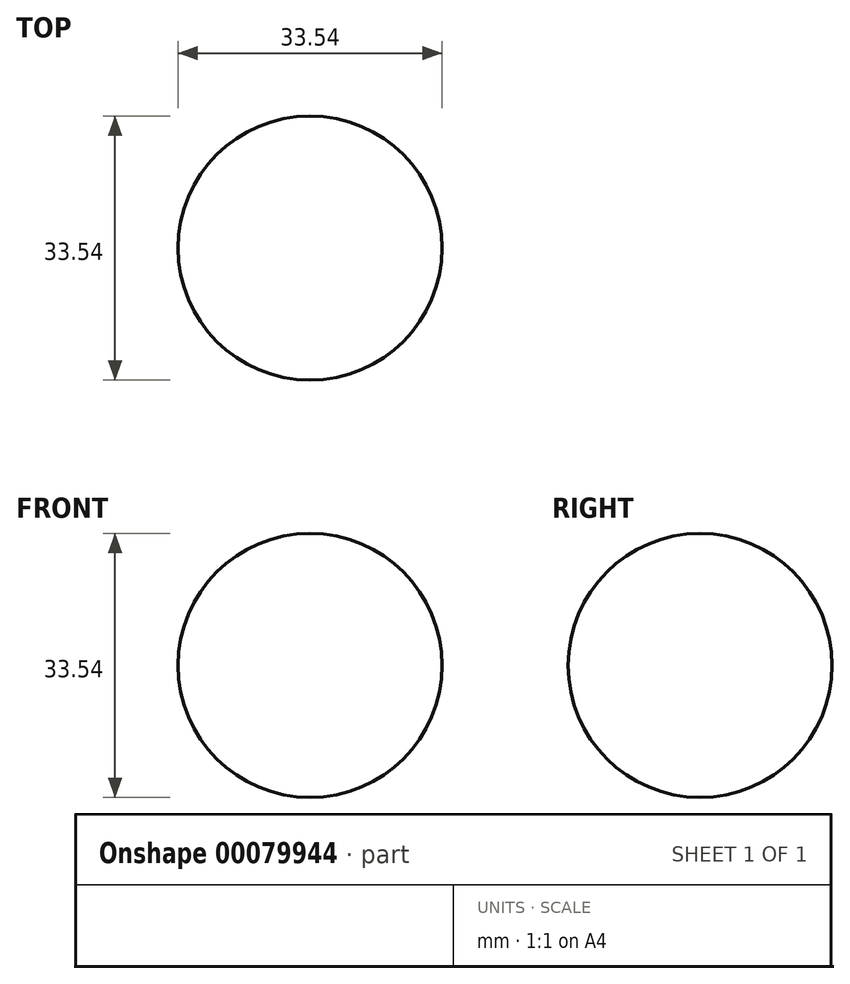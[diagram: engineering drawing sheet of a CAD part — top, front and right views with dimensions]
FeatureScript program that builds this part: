
annotation { "Feature Type Name" : "Feature", "Feature Type Description" : "" }
export const myFeature = defineFeature(function(context is Context, id is Id, definition is map)
    precondition{}
    {
        {
            var Q0;
            Q0=qCreatedBy(makeId("Top.planeOp"),FACE);
            var sketch = newSketch(context, id + "F0", { "sketchPlane" : qUnion([Q0])});
            skArc(sketch, "E0", {"start": v(16.77, 0) * mm, "mid": v(0, 16.77) * mm, "end": v(-16.77, 0) * mm});
            skLineSegment(sketch, "E1", {"start": v(-16.77, 0) * mm, "end": v(16.77, 0) * mm});
            skSolve(sketch);
        }
        {
            var Q0;
            Q0=makeQuery(id+"F0.imprint","IMPRINT",FACE,{"disambiguationData":[TD([[makeQuery(id+"F0.imprint","IMPRINT",EDGE,{"derivedFrom":sQuery(id+"F0.wireOp",EDGE,"E0")}),1.0]])]});
            var Q1;
            Q1=sQuery(id+"F0.wireOp",EDGE,"E1");
            revolve(context, id + "F1", {"entities" : qUnion([Q0]), "axis" : qUnion([Q1]), "revolveType" : RevolveType.FULL});
        }
    });
